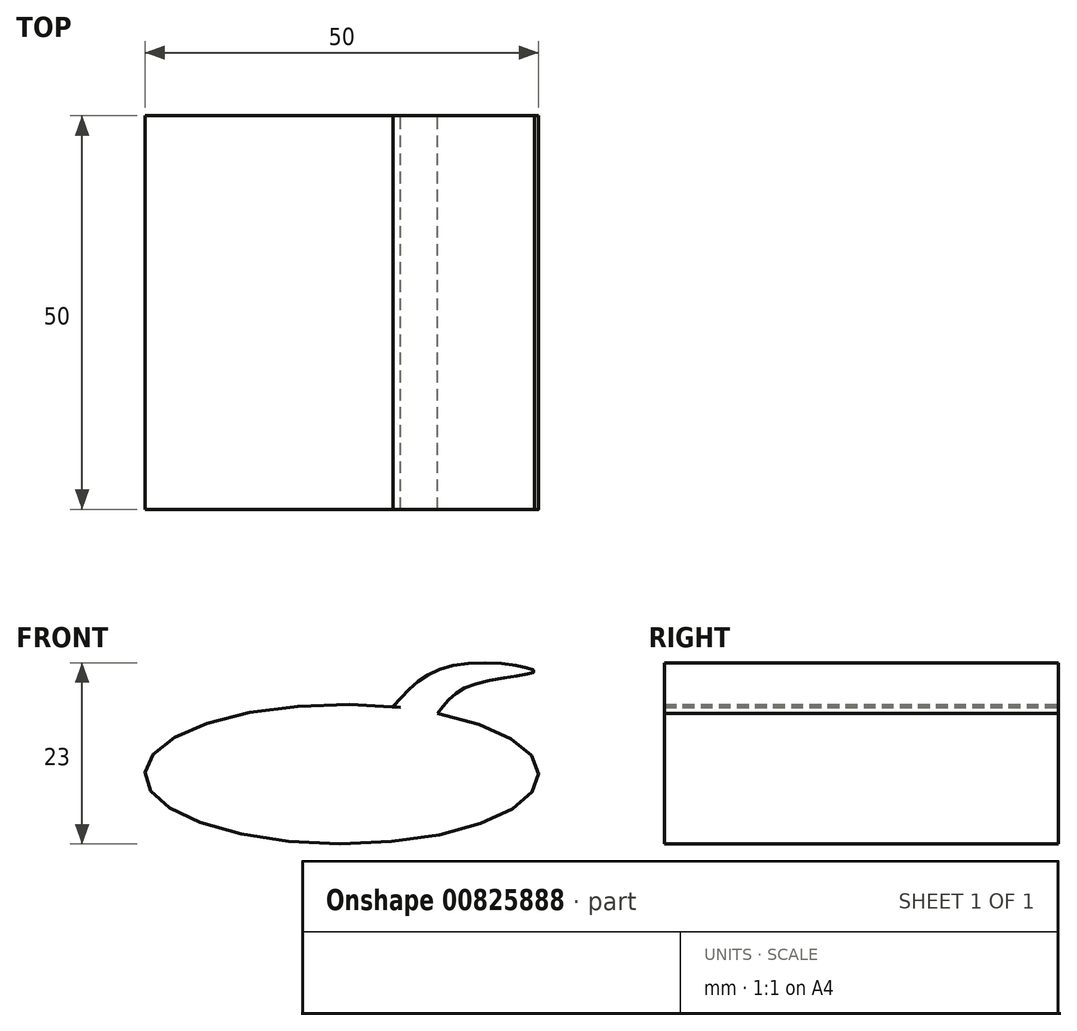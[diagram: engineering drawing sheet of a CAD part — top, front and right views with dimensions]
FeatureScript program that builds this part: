
annotation { "Feature Type Name" : "Feature", "Feature Type Description" : "" }
export const myFeature = defineFeature(function(context is Context, id is Id, definition is map)
    precondition{}
    {
        {
            var Q0;
            Q0=qCreatedBy(makeId("Front.planeOp"),FACE);
            var sketch = newSketch(context, id + "F0", { "sketchPlane" : qUnion([Q0])});
            skEllipse(sketch, "E0", {"center": v(0, 0) * mm, "majorRadius": 25 * mm, "minorRadius": 8.85 * mm, "majorAxis": v(1, 0)});
            skSolve(sketch);
        }
        {
            var Q0;
            Q0=makeQuery(id+"F0.imprint","IMPRINT",FACE,{"disambiguationData":[TD([[makeQuery(id+"F0.imprint","IMPRINT",EDGE,{"derivedFrom":sQuery(id+"F0.wireOp",EDGE,"E0")}),1.0]])]});
            extrude(context, id + "F1", {"entities" : qUnion([Q0]), "depth" : 50 * mm, "offsetDistance" : 25.4 * mm});
        }
        {
            var Q0;
            Q0=qCreatedBy(makeId("Front.planeOp"),FACE);
            var sketch = newSketch(context, id + "F2", { "sketchPlane" : qUnion([Q0])});
            skFitSpline(sketch, "E1", {"points": [v(6.52, 8.6) * mm, v(14.5, 13.9) * mm, v(24.46, 13.07) * mm, v(16.79, 11.41) * mm, v(12.12, 7.68) * mm], "startDerivative": vector(22.64, 25.63) * mm, "endDerivative": vector(-15.21, -20.38) * mm});
            skLineSegment(sketch, "E2", {"start": v(6.52, 8.6) * mm, "end": v(12.12, 7.68) * mm});
            skSolve(sketch);
        }
        {
            var Q0;
            Q0=makeQuery(id+"F2.imprint","IMPRINT",FACE,{"disambiguationData":[TD([[makeQuery(id+"F2.imprint","IMPRINT",EDGE,{"derivedFrom":sQuery(id+"F2.wireOp",EDGE,"E1")}),-1.0]])]});
            var Q1;
            Q1=sQuery(id+"F2.wireOp",EDGE,"E1");
            extrude(context, id + "F3", {"entities" : qUnion([Q0]), "operationType" : NewBodyOperationType.ADD, "surfaceEntities" : qUnion([Q1]), "depth" : 50 * mm, "offsetDistance" : 25.4 * mm});
        }
    });
